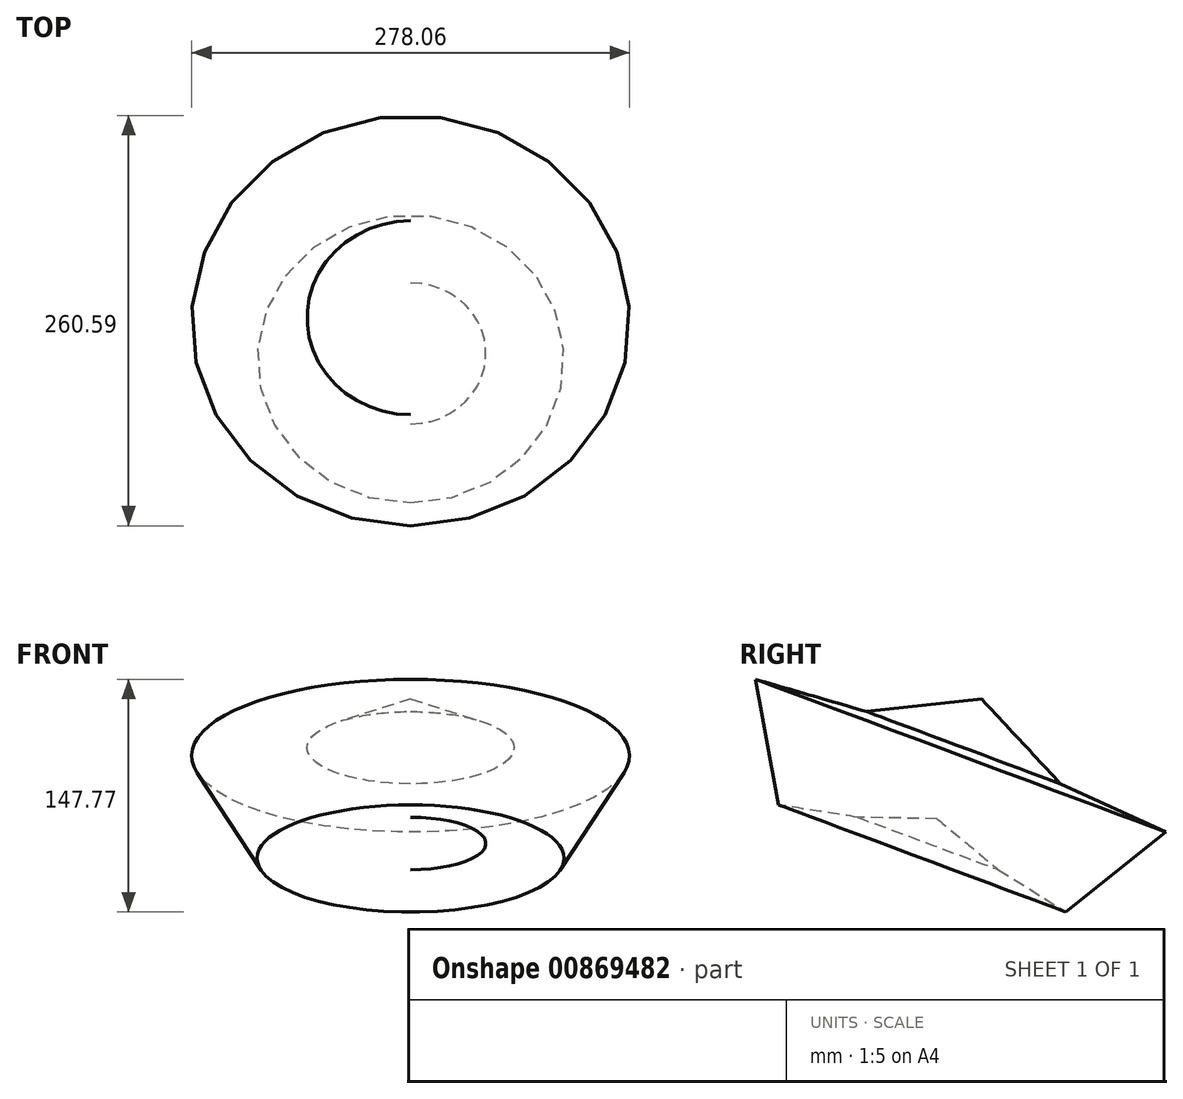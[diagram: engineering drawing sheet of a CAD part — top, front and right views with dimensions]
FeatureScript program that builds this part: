
annotation { "Feature Type Name" : "Feature", "Feature Type Description" : "" }
export const myFeature = defineFeature(function(context is Context, id is Id, definition is map)
    precondition{}
    {
        {
            var Q0;
            Q0=qCreatedBy(makeId("Right.planeOp"),FACE);
            var sketch = newSketch(context, id + "F0", { "sketchPlane" : qUnion([Q0])});
            skLineSegment(sketch, "E0", {"start": v(35.42, 19.28) * mm, "end": v(-35.17, 39.78) * mm});
            skLineSegment(sketch, "E1", {"start": v(-35.17, 39.78) * mm, "end": v(-20.49, -40) * mm});
            skLineSegment(sketch, "E2", {"start": v(-20.49, -40) * mm, "end": v(29.56, -47.8) * mm});
            skLineSegment(sketch, "E3.MirrorCS", {"start": v(35.42, 19.28) * mm, "end": v(108.5, 27.22) * mm});
            skLineSegment(sketch, "E4.MirrorCS", {"start": v(108.5, 27.22) * mm, "end": v(80.2, -48.8) * mm});
            skLineSegment(sketch, "E5.MirrorCS", {"start": v(80.2, -48.8) * mm, "end": v(29.56, -47.8) * mm});
            skSolve(sketch);
        }
        {
            var Q0;
            Q0 = qSketchRegion(id + "F0", true);
            var Q1;
            Q1=sQuery(id+"F0.wireOp",EDGE,"E4.MirrorCS");
            revolve(context, id + "F1", {"surfaceOperationType" : NewSurfaceOperationType.NEW, "entities" : qUnion([Q0]), "axis" : qUnion([Q1]), "revolveType" : RevolveType.FULL});
        }
    });
